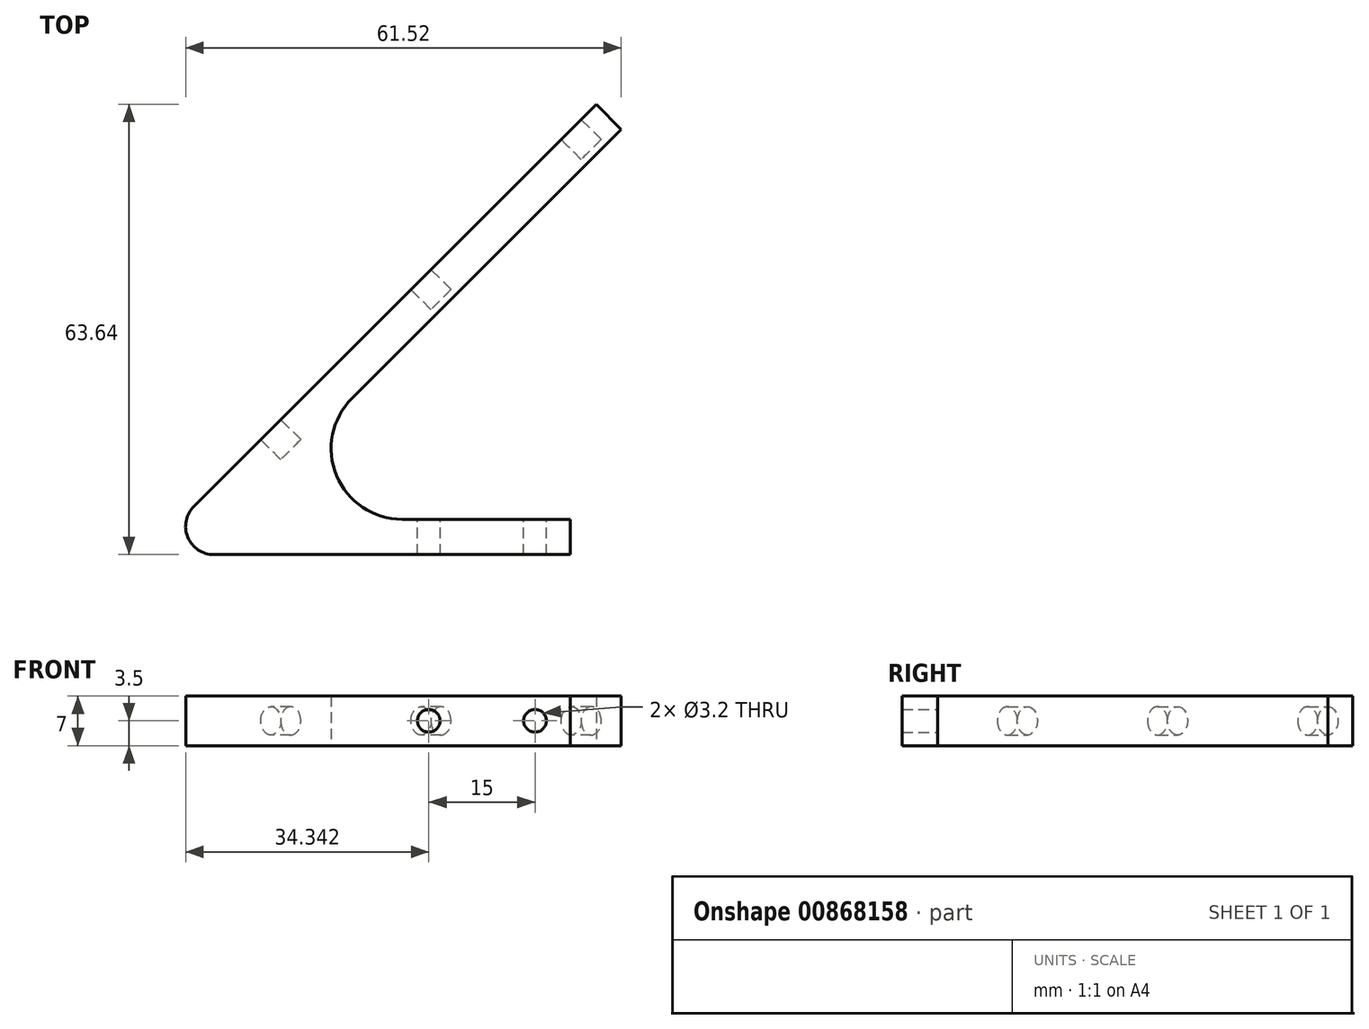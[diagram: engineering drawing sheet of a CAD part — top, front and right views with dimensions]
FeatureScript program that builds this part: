
annotation { "Feature Type Name" : "Feature", "Feature Type Description" : "" }
export const myFeature = defineFeature(function(context is Context, id is Id, definition is map)
    precondition{}
    {
        {
            var Q0;
            Q0=qCreatedBy(makeId("Top.planeOp"),FACE);
            var sketch = newSketch(context, id + "F0", { "sketchPlane" : qUnion([Q0])});
            skLineSegment(sketch, "E0", {"start": v(28.81, 63.64) * mm, "end": v(-28, 6.83) * mm});
            skLineSegment(sketch, "E1", {"start": v(-25.17, 0) * mm, "end": v(25.17, 0) * mm});
            skLineSegment(sketch, "E2.0", {"start": v(1.38, 5) * mm, "end": v(25.17, 5) * mm});
            skLineSegment(sketch, "E2.1", {"start": v(32.35, 60.1) * mm, "end": v(-5.69, 22.07) * mm});
            skLineSegment(sketch, "E3", {"start": v(25.17, 5) * mm, "end": v(25.17, 0) * mm});
            skLineSegment(sketch, "E4", {"start": v(28.81, 63.64) * mm, "end": v(32.35, 60.1) * mm});
            skPoint(sketch, "E5.visualSharp", {"position": v(-22.76, 5) * mm});
            skArc(sketch, "E5.filletArc", {"start": v(-5.69, 22.07) * mm, "mid": v(-7.85, 11.17) * mm, "end": v(1.38, 5) * mm});
            skPoint(sketch, "E6.visualSharp", {"position": v(-34.83, 0) * mm});
            skArc(sketch, "E6.filletArc", {"start": v(-28, 6.83) * mm, "mid": v(-28.87, 2.47) * mm, "end": v(-25.17, 0) * mm});
            skSolve(sketch);
        }
        {
            var Q0;
            Q0 = qSketchRegion(id + "F0", true);
            extrude(context, id + "F1", {"entities" : qUnion([Q0]), "depth" : 7 * mm, "offsetDistance" : 25 * mm});
        }
        {
            var Q0;
            Q0=makeQuery(id+"F1.opExtrude","SWEPT_FACE",FACE,{"disambiguationData":[OSD([sQuery(id+"F0.wireOp",EDGE,"E0")])]});
            var sketch = newSketch(context, id + "F2", { "sketchPlane" : qUnion([Q0])});
            skCircle(sketch, "E7", {"center": v(-0.37, 3.5) * mm, "radius": 2 * mm});
            skCircle(sketch, "E8.MirrorC", {"center": v(-60.37, 3.5) * mm, "radius": 2 * mm});
            skCircle(sketch, "E9", {"center": v(-30.37, 3.5) * mm, "radius": 2 * mm});
            skLineSegment(sketch, "E10", {"start": v(-65.37, 3.5) * mm, "end": v(14.97, 3.5) * mm, "construction": true});
            skSolve(sketch);
        }
        {
            var Q0;
            Q0 = qSketchRegion(id + "F2", true);
            var Q1;
            Q1=makeQuery(id+"F1.opExtrude","SWEPT_FACE",FACE,{"disambiguationData":[OSD([sQuery(id+"F0.wireOp",EDGE,"E2.1")])]});
            extrude(context, id + "F3", {"entities" : qUnion([Q0]), "operationType" : NewBodyOperationType.REMOVE, "endBound" : BoundingType.UP_TO_SURFACE, "oppositeDirection" : true, "depth" : 3.4 * mm, "endBoundEntityFace" : qUnion([Q1]), "hasOffset" : true, "offsetDistance" : 1 * mm});
        }
        {
            var Q0;
            Q0=makeQuery(id+"F1.opExtrude","SWEPT_FACE",FACE,{"disambiguationData":[OSD([sQuery(id+"F0.wireOp",EDGE,"E2.0")])]});
            var sketch = newSketch(context, id + "F4", { "sketchPlane" : qUnion([Q0])});
            skLineSegment(sketch, "E11", {"start": v(-25.17, 3.5) * mm, "end": v(-1.38, 3.5) * mm, "construction": true});
            skCircle(sketch, "E12", {"center": v(-20.17, 3.5) * mm, "radius": 1.6 * mm});
            skCircle(sketch, "E13", {"center": v(-5.17, 3.5) * mm, "radius": 1.6 * mm});
            skSolve(sketch);
        }
        {
            var Q0;
            Q0 = qSketchRegion(id + "F4", true);
            var Q1;
            Q1=makeQuery(id+"F1.opExtrude","SWEPT_FACE",FACE,{"disambiguationData":[OSD([sQuery(id+"F0.wireOp",EDGE,"E1")])]});
            extrude(context, id + "F5", {"entities" : qUnion([Q0]), "operationType" : NewBodyOperationType.REMOVE, "endBound" : BoundingType.UP_TO_SURFACE, "oppositeDirection" : true, "depth" : 25 * mm, "endBoundEntityFace" : qUnion([Q1]), "offsetDistance" : 25 * mm});
        }
    });
